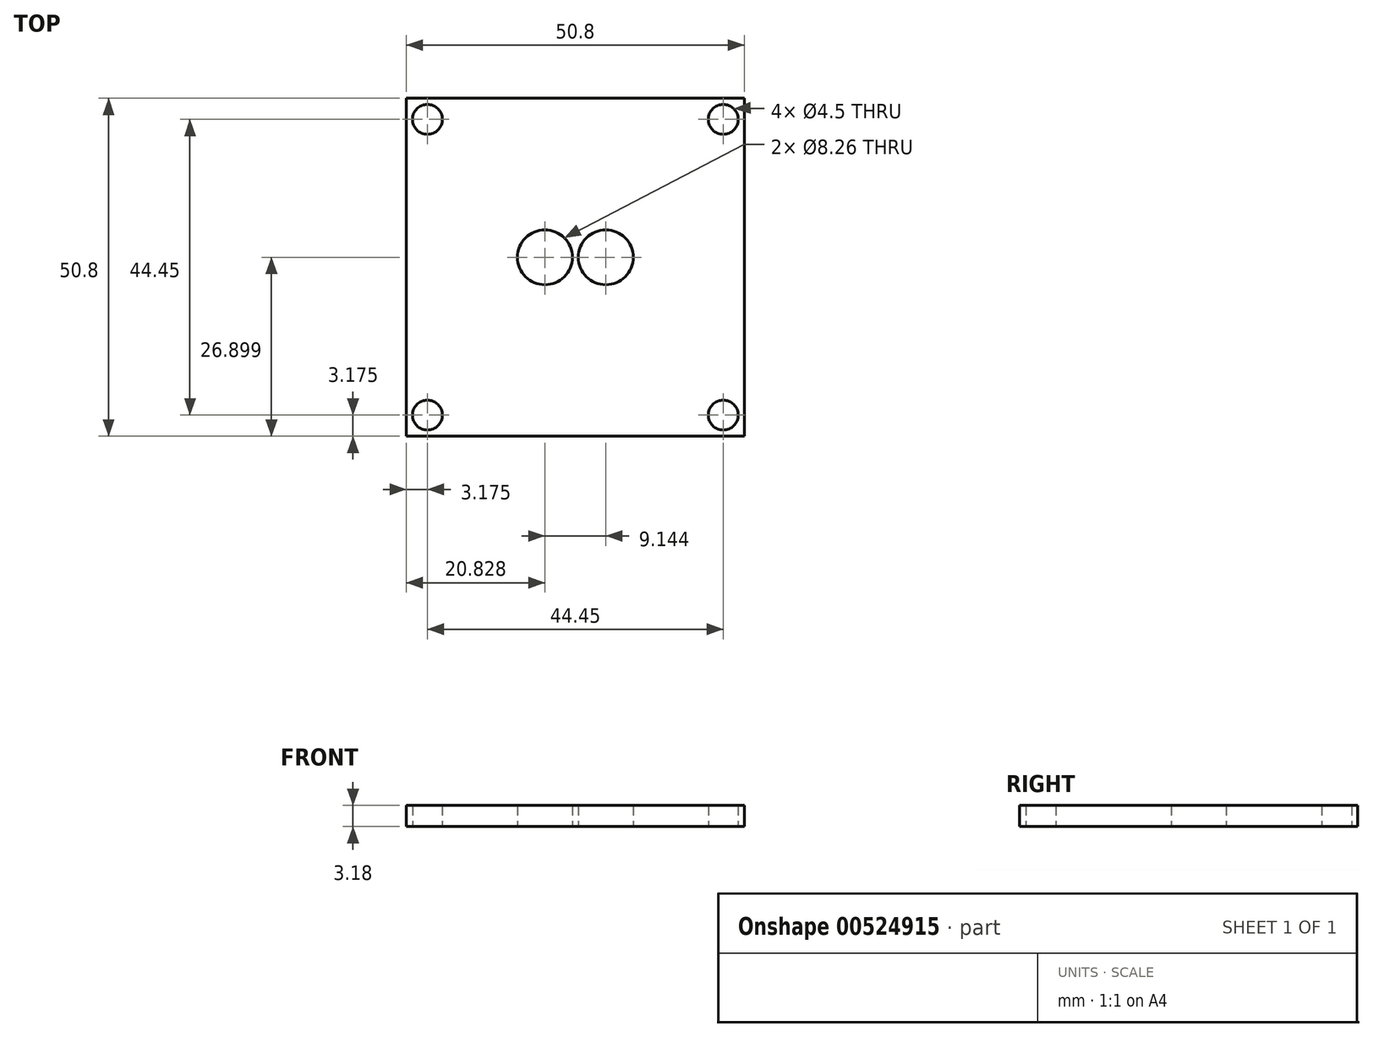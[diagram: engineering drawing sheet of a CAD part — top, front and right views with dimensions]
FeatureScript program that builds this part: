
annotation { "Feature Type Name" : "Feature", "Feature Type Description" : "" }
export const myFeature = defineFeature(function(context is Context, id is Id, definition is map)
    precondition{}
    {
        {
            var Q0;
            Q0=qCreatedBy(makeId("Top.planeOp"),FACE);
            var sketch = newSketch(context, id + "F0", { "sketchPlane" : qUnion([Q0])});
            skLineSegment(sketch, "E0.bottom", {"start": v(25.4, 25.4) * mm, "end": v(-25.4, 25.4) * mm});
            skLineSegment(sketch, "E0.top", {"start": v(25.4, -25.4) * mm, "end": v(-25.4, -25.4) * mm});
            skLineSegment(sketch, "E0.left", {"start": v(25.4, 25.4) * mm, "end": v(25.4, -25.4) * mm});
            skLineSegment(sketch, "E0.right", {"start": v(-25.4, 25.4) * mm, "end": v(-25.4, -25.4) * mm});
            skPoint(sketch, "E0.middle", {"position": v(0, 0) * mm});
            skLineSegment(sketch, "E1", {"start": v(-35.53, 1.5) * mm, "end": v(47.28, 1.5) * mm, "construction": true});
            skCircle(sketch, "E2", {"center": v(4.57, 1.5) * mm, "radius": 4.13 * mm});
            skCircle(sketch, "E3.MirrorC", {"center": v(-4.57, 1.5) * mm, "radius": 4.13 * mm});
            skCircle(sketch, "E4", {"center": v(-22.23, 22.23) * mm, "radius": 2.25 * mm});
            skCircle(sketch, "E5.MirrorC", {"center": v(22.23, 22.23) * mm, "radius": 2.25 * mm});
            skCircle(sketch, "E6.MirrorC", {"center": v(-22.23, -22.23) * mm, "radius": 2.25 * mm});
            skCircle(sketch, "E7.MirrorC", {"center": v(22.23, -22.23) * mm, "radius": 2.25 * mm});
            skSolve(sketch);
        }
        {
            var Q0;
            Q0 = qSketchRegion(id + "F0", true);
            extrude(context, id + "F1", {"entities" : qUnion([Q0]), "depth" : 3.17 * mm, "offsetDistance" : 25 * mm});
        }
    });
